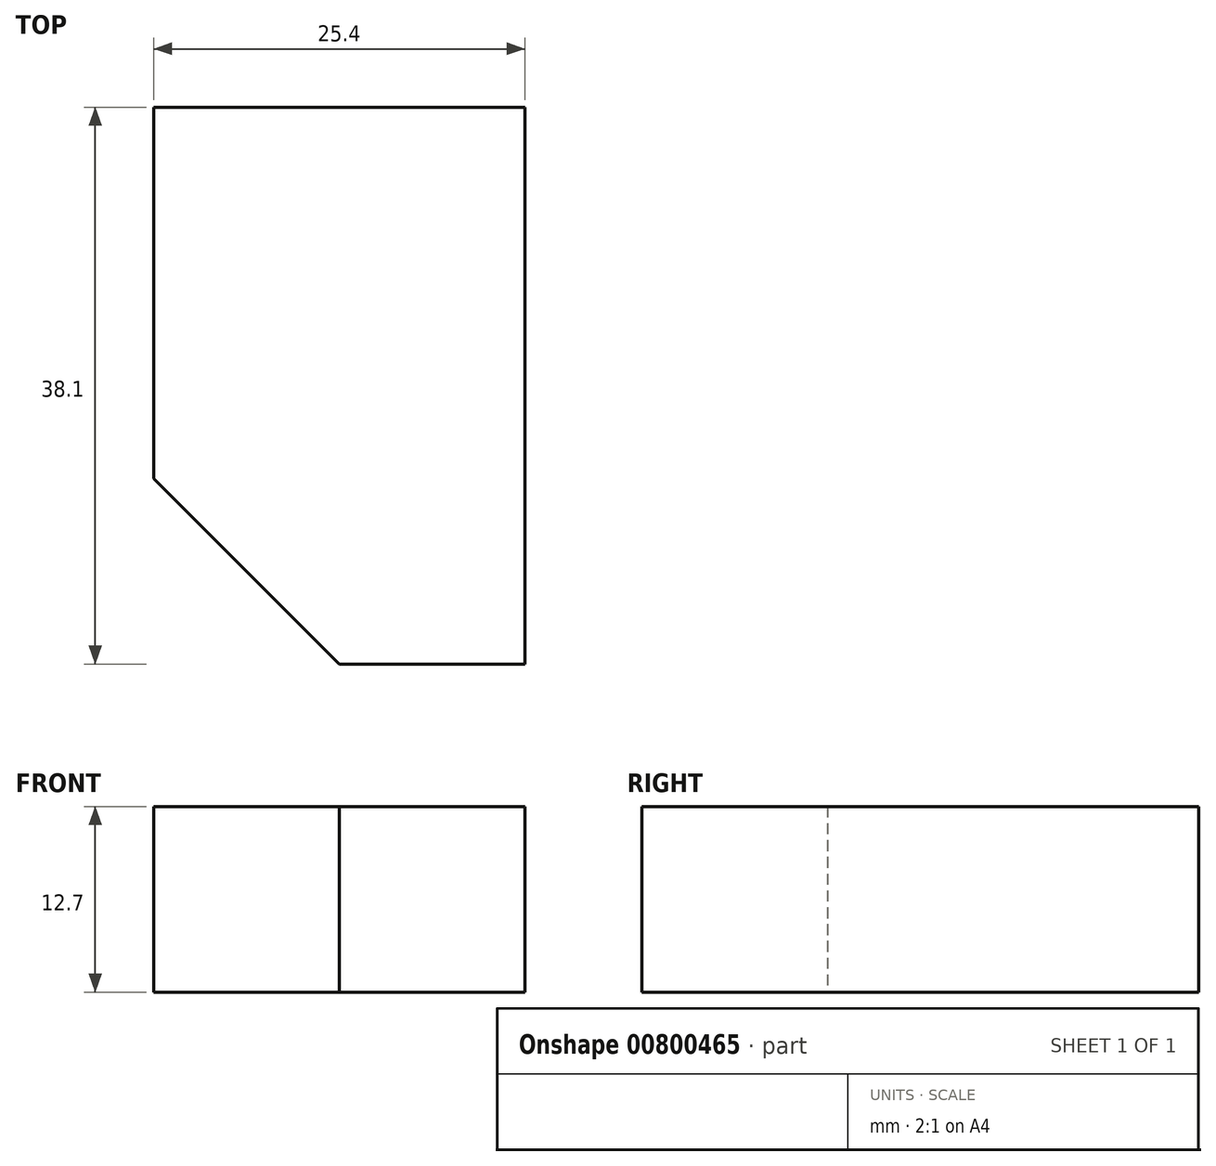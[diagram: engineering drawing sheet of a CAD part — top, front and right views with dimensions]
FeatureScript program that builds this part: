
annotation { "Feature Type Name" : "Feature", "Feature Type Description" : "" }
export const myFeature = defineFeature(function(context is Context, id is Id, definition is map)
    precondition{}
    {
        {
            var Q0;
            Q0=qCreatedBy(makeId("Top.planeOp"),FACE);
            var sketch = newSketch(context, id + "F0", { "sketchPlane" : qUnion([Q0])});
            skLineSegment(sketch, "E0", {"start": v(0, 0) * mm, "end": v(0, 25.4) * mm});
            skLineSegment(sketch, "E1", {"start": v(0, 25.4) * mm, "end": v(25.4, 25.4) * mm});
            skLineSegment(sketch, "E2", {"start": v(25.4, 25.4) * mm, "end": v(25.4, -12.7) * mm});
            skLineSegment(sketch, "E3", {"start": v(25.4, -12.7) * mm, "end": v(12.7, -12.7) * mm});
            skPoint(sketch, "E4.endSnap0", {"position": v(19.05, -12.7) * mm});
            skLineSegment(sketch, "E5", {"start": v(12.7, -12.7) * mm, "end": v(0, 0) * mm});
            skSolve(sketch);
        }
        {
            var Q0;
            Q0=makeQuery(id+"F0.imprint","IMPRINT",FACE,{"disambiguationData":[TD([[makeQuery(id+"F0.imprint","IMPRINT",EDGE,{"derivedFrom":sQuery(id+"F0.wireOp",EDGE,"E0")}),-1.0]])]});
            extrude(context, id + "F1", {"entities" : qUnion([Q0]), "depth" : 12.7 * mm, "offsetDistance" : 25.4 * mm});
        }
    });
